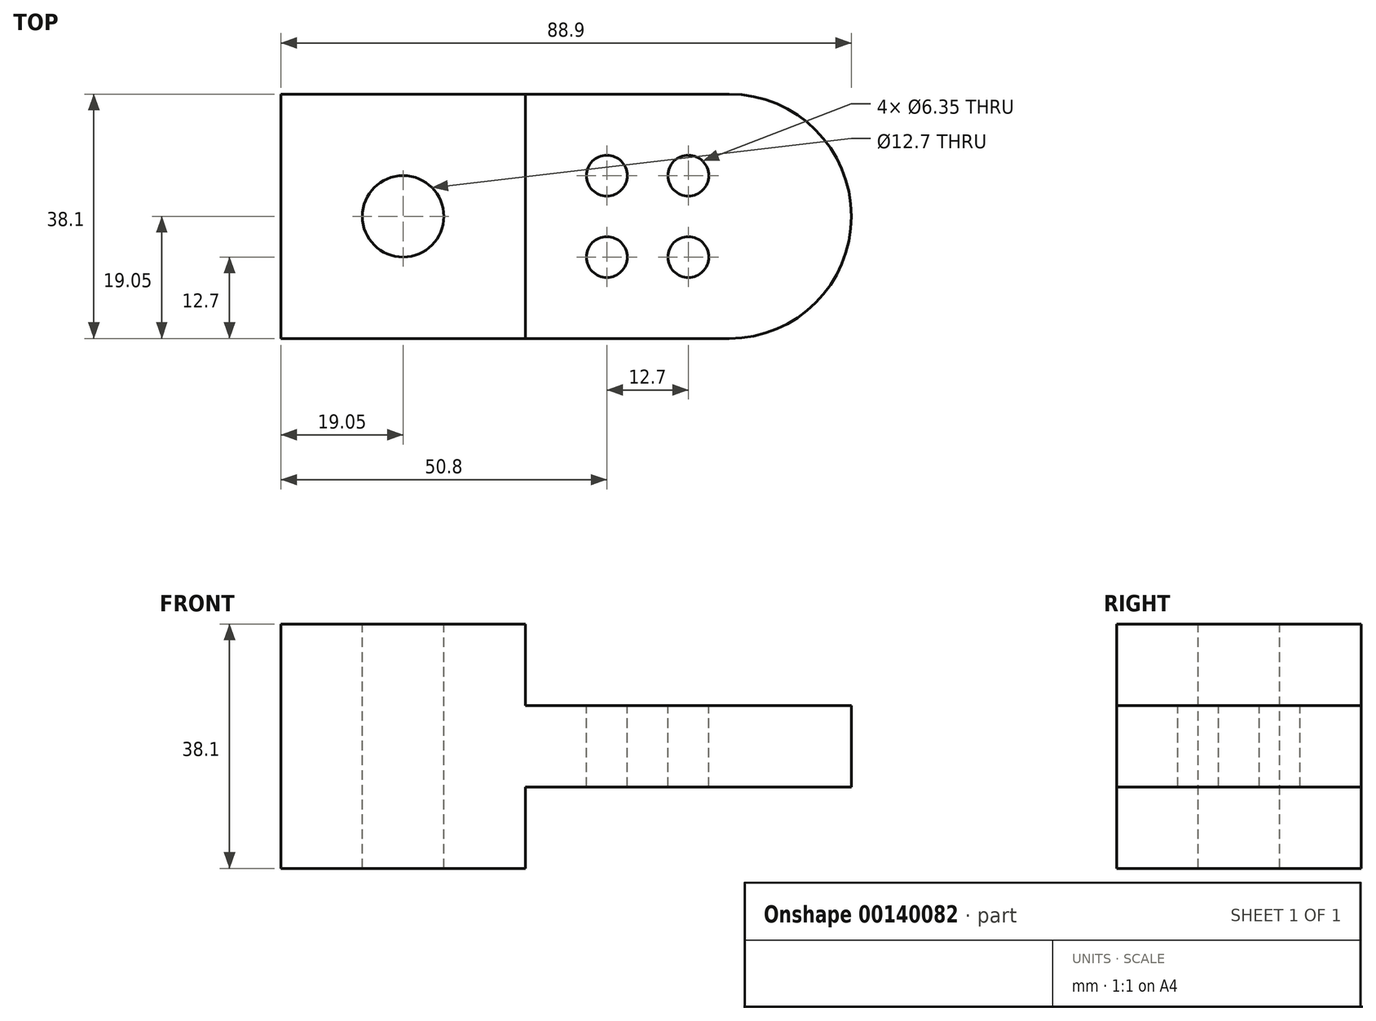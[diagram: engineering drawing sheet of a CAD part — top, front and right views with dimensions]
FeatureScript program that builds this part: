
annotation { "Feature Type Name" : "Feature", "Feature Type Description" : "" }
export const myFeature = defineFeature(function(context is Context, id is Id, definition is map)
    precondition{}
    {
        {
            var Q0;
            Q0=qCreatedBy(makeId("Top.planeOp"),FACE);
            var sketch = newSketch(context, id + "F0", { "sketchPlane" : qUnion([Q0])});
            skLineSegment(sketch, "E0", {"start": v(0, 19.05) * mm, "end": v(38.1, 19.05) * mm});
            skLineSegment(sketch, "E1", {"start": v(38.1, 19.05) * mm, "end": v(69.85, 19.05) * mm});
            skLineSegment(sketch, "E2", {"start": v(0, 19.05) * mm, "end": v(0, 0) * mm});
            skLineSegment(sketch, "E3", {"start": v(0, 0) * mm, "end": v(0, -19.05) * mm});
            skLineSegment(sketch, "E4", {"start": v(0, -19.05) * mm, "end": v(38.1, -19.05) * mm});
            skLineSegment(sketch, "E5", {"start": v(38.1, -19.05) * mm, "end": v(69.85, -19.05) * mm});
            skArc(sketch, "E6", {"start": v(69.85, -19.05) * mm, "mid": v(88.9, 0) * mm, "end": v(69.85, 19.05) * mm});
            skLineSegment(sketch, "E7", {"start": v(38.1, 19.05) * mm, "end": v(38.1, -19.05) * mm});
            skSolve(sketch);
        }
        {
            var Q0;
            Q0=makeQuery(id+"F0.imprint","IMPRINT",FACE,{"disambiguationData":[TD([[makeQuery(id+"F0.imprint","IMPRINT",EDGE,{"derivedFrom":sQuery(id+"F0.wireOp",EDGE,"E0")}),-1.0]])]});
            extrude(context, id + "F1", {"entities" : qUnion([Q0]), "endBound" : BoundingType.SYMMETRIC, "depth" : 38.1 * mm});
        }
        {
            var Q0;
            Q0=makeQuery(id+"F0.imprint","IMPRINT",FACE,{"disambiguationData":[TD([[makeQuery(id+"F0.imprint","IMPRINT",EDGE,{"derivedFrom":sQuery(id+"F0.wireOp",EDGE,"E1")}),-1.0]])]});
            extrude(context, id + "F2", {"entities" : qUnion([Q0]), "operationType" : NewBodyOperationType.ADD, "endBound" : BoundingType.SYMMETRIC, "depth" : 2 * 6.35 * mm});
        }
        {
            var Q0;
            Q0=makeQuery(id+"F1.opExtrude","CAP_FACE",FACE,{"disambiguationData":[OSD([sQuery(id+"F0.wireOp",EDGE,"E0"),sQuery(id+"F0.wireOp",EDGE,"E2"),sQuery(id+"F0.wireOp",EDGE,"E3"),sQuery(id+"F0.wireOp",EDGE,"E4"),sQuery(id+"F0.wireOp",EDGE,"E7")])],"isStart":false});
            var sketch = newSketch(context, id + "F3", { "sketchPlane" : qUnion([Q0])});
            skLineSegment(sketch, "E8", {"start": v(0, 0) * mm, "end": v(19.05, 0) * mm, "construction": true});
            skLineSegment(sketch, "E9", {"start": v(38.1, 19.05) * mm, "end": v(50.8, 19.05) * mm, "construction": true});
            skLineSegment(sketch, "E10", {"start": v(50.8, 19.05) * mm, "end": v(50.8, 6.35) * mm, "construction": true});
            skLineSegment(sketch, "E11", {"start": v(50.8, 6.35) * mm, "end": v(50.8, -6.35) * mm, "construction": true});
            skLineSegment(sketch, "E12", {"start": v(50.8, -6.35) * mm, "end": v(63.5, -6.35) * mm, "construction": true});
            skLineSegment(sketch, "E13", {"start": v(63.5, -6.35) * mm, "end": v(63.5, 6.35) * mm, "construction": true});
            skSolve(sketch);
        }
        {
            var Q0;
            Q0=sQuery(id+"F3.wireOp",VERTEX,"E8.end");
            var Q1;
            Q1=makeQuery(id+"F1.opExtrude","SWEPT_BODY",BODY,{"disambiguationData":[OSD([sQuery(id+"F0.wireOp",EDGE,"E0"),sQuery(id+"F0.wireOp",EDGE,"E2"),sQuery(id+"F0.wireOp",EDGE,"E3"),sQuery(id+"F0.wireOp",EDGE,"E4"),sQuery(id+"F0.wireOp",EDGE,"E7")])]});
            hole(context, id + "F4", {"style" : HoleStyle.SIMPLE, "endStyle" : HoleEndStyle.THROUGH, "holeDiameter" : 12.7 * mm, "locations" : qUnion([Q0]), "scope" : qUnion([Q1]), "isTappedThrough" : true});
        }
        {
            var Q0;
            Q0=sQuery(id+"F3.wireOp",VERTEX,"E11.start");
            var Q1;
            Q1=sQuery(id+"F3.wireOp",VERTEX,"E13.end");
            var Q2;
            Q2=sQuery(id+"F3.wireOp",VERTEX,"E13.start");
            var Q3;
            Q3=sQuery(id+"F3.wireOp",VERTEX,"E12.start");
            var Q4;
            Q4=makeQuery(id+"F1.opExtrude","SWEPT_BODY",BODY,{"disambiguationData":[OSD([sQuery(id+"F0.wireOp",EDGE,"E0"),sQuery(id+"F0.wireOp",EDGE,"E2"),sQuery(id+"F0.wireOp",EDGE,"E3"),sQuery(id+"F0.wireOp",EDGE,"E4"),sQuery(id+"F0.wireOp",EDGE,"E7")])]});
            hole(context, id + "F5", {"style" : HoleStyle.SIMPLE, "endStyle" : HoleEndStyle.THROUGH, "holeDiameter" : 6.35 * mm, "locations" : qUnion([Q0, Q1, Q2, Q3]), "scope" : qUnion([Q4]), "isTappedThrough" : true});
        }
    });
